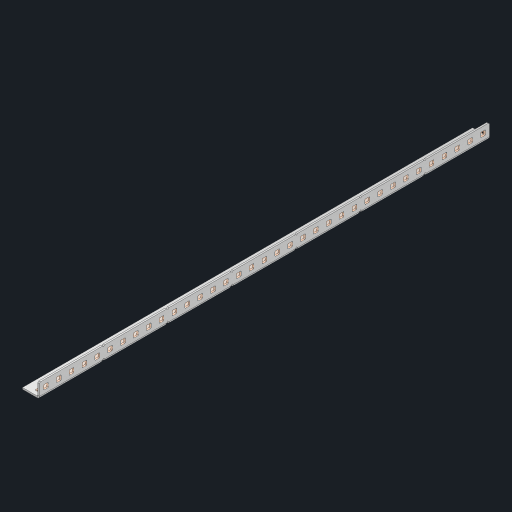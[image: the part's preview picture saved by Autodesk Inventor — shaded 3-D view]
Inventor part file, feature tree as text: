
AUTODESK INVENTOR PART (.ipt)
format: ipt  version: 2023 (Build 270158000, 158)  size: 1,058,816 bytes
history: native  units: in
note: dims shown in document units (in); Inventor stores cm internally (conversion verified against a paired STEP export)
features: other x75, extrude x69, sheet_metal_op x10, sketch x8, mirror x1, pattern_linear x1, chamfer x1
ambient origin geometry x8: Origin, YZ Plane, XZ Plane, XY Plane, X Axis, Y Axis, Z Axis, Center Point
bodies: Solid1 (feature_tree), Body (feature_tree)
feature tree (165):
  other  "Flange Pattern Plane"
  sheet_metal_op  "Flange Pattern"
  sheet_metal_op  "Body Pattern"
  other  "Arc Length"
  mirror  "Notch Mirror"
  pattern_linear  "Notch Pattern"  Spacing1=0.25in  [1 undecoded]
  chamfer  "End Chamfer"
  extrude  "Half Cut"  Depth=0.0625in
  sketch  "Sketch1"  dims[d0=1.5in]
  other  "Plate1"
  sketch  "Sketch2"  dims[d1=17.5in]
  other  "Plate2"
  sheet_metal_op  "Bend1"
  sheet_metal_op  "Corner1"
  sketch  "Sketch3"  dims[d2=0.0625in]
  other  "Flange Pattern Sketch"
  sketch  "Sketch7"  dims[d3=0.0625in]
  other  "Srf1"
  other  "Srf2"
  sketch  "Sketch8"  dims[d4=0.0312in]
  sketch  "Sketch9"  dims[d5=0.125in]
  other  "Srf91"
  sheet_metal_op  "Body Pattern Sketch"
  other  "Srf92"
  sketch  "Sketch13"  dims[d6=0.0625in]
  sketch  "Sketch14"  dims[d7=0.5in d8=90.0deg d9=0.0312in d10=0.25in d11=0.0625in d12=0.0625in d16=0.182in d17=0.02in d18=0.0625in d19=0.0in d20=0.25in d21=0.25in d46=0.172in d47=1.0in d48=0.0in d49=0.182in d50=0.02in d51=0.25in d52=0.25in d53=0.0625in d54=0.0in d55=0.172in d56=1.0in d57=0.0in d60=13.7795in d62=0.5in d63=0.3937in d65=0.5in d85=0.1473in d86=0.1782in d88=0.04in d89=0.0625in d90=0.0in d91=0.04in d92=0.0491in d95=2.5in d96=0.04in d97=0.25in d98=45.0deg d101=0.0in d102=2.497in d131=0.5in d132=13.7795in d134=0.5in d139=0.5in]
  other  "Srf856"
  other  "Srf1310"
  other  "Srf1311"
  other  "Srf1312"
  other  "Srf1376"
  other  "Srf1377"
  other  "Srf1728"
  other  "Srf1755"
  other  "Srf1878"
  other  "Srf1879"
  other  "Srf1880"
  other  "Srf1881"
  other  "Srf1882"
  other  "Srf1883"
  other  "Srf1884"
  other  "Srf1885"
  other  "Srf1886"
  other  "Srf1887"
  other  "Srf1888"
  other  "Srf1889"
  other  "Srf1890"
  other  "Srf1891"
  other  "Srf1892"
  other  "Srf1893"
  other  "Srf1894"
  other  "Srf1895"
  other  "Srf1896"
  other  "Srf1897"
  other  "Srf1898"
  other  "Srf1899"
  other  "Srf1900"
  other  "Srf1901"
  other  "Srf1902"
  other  "Srf1903"
  other  "Srf1904"
  other  "Srf1905"
  other  "Srf1906"
  other  "Srf1942"
  other  "Srf1943"
  other  "Srf1944"
  other  "Srf1945"
  other  "Srf1946"
  other  "Srf1947"
  other  "Srf1948"
  other  "Srf1949"
  other  "Srf1950"
  other  "Srf1951"
  other  "Srf1952"
  other  "Srf1953"
  other  "Srf1954"
  other  "Srf1955"
  other  "Srf1956"
  other  "Srf1957"
  other  "Srf1958"
  other  "Srf1959"
  other  "Srf1960"
  other  "Srf1961"
  other  "Srf1962"
  other  "Srf1963"
  other  "Srf1964"
  other  "Srf1965"
  other  "Srf1966"
  other  "Srf1967"
  other  "Srf1968"
  other  "Srf1969"
  other  "Srf1970"
  sheet_metal_op  "Flange Stamp"
  sheet_metal_op  "Flange Circle"
  sheet_metal_op  "Body Stamp"
  sheet_metal_op  "Body Circle"
  sheet_metal_op  "Notch"
  extrude  "ExtrusionSrf2"  Depth=0.0625in
  extrude  "ExtrusionSrf92"  Depth=0.5in
  extrude  "ExtrusionSrf856"  Depth=0.02in
  extrude  "ExtrusionSrf1310"  Depth=0.0625in
  extrude  "ExtrusionSrf1311"  TaperAngle=0.0deg  [1 undecoded]
  extrude  "ExtrusionSrf1312"  Depth=0.5in
  extrude  "ExtrusionSrf1376"  Depth=0.5in
  extrude  "ExtrusionSrf1377"  Depth=0.5in
  extrude  "ExtrusionSrf1728"  Depth=0.5in TaperAngle=0.0deg
  extrude  "ExtrusionSrf1755"  Depth=0.5in
  extrude  "ExtrusionSrf1878"  Depth=0.02in
  extrude  "ExtrusionSrf1879"  Depth=0.5in
  extrude  "ExtrusionSrf1880"  Depth=0.5in
  extrude  "ExtrusionSrf1881"  Depth=0.0625in
  extrude  "ExtrusionSrf1882"  TaperAngle=0.0deg  [1 undecoded]
  extrude  "ExtrusionSrf1883"  Depth=0.5in
  extrude  "ExtrusionSrf1884"  Depth=0.5in TaperAngle=0.0deg
  extrude  "ExtrusionSrf1885"  Depth=0.5in
  extrude  "ExtrusionSrf1886"  Depth=0.5in
  extrude  "ExtrusionSrf1887"  Depth=0.5in
  extrude  "ExtrusionSrf1888"  Depth=0.5in
  extrude  "ExtrusionSrf1889"  Depth=0.5in
  extrude  "ExtrusionSrf1890"  Depth=0.0625in
  extrude  "ExtrusionSrf1891"  TaperAngle=0.0deg  [1 undecoded]
  extrude  "ExtrusionSrf1892"  Depth=0.5in
  extrude  "ExtrusionSrf1893"  Depth=0.5in
  extrude  "ExtrusionSrf1894"  Depth=0.5in
  extrude  "ExtrusionSrf1895"  Depth=0.5in TaperAngle=45.0deg
  extrude  "ExtrusionSrf1896"  TaperAngle=0.0deg  [1 undecoded]
  extrude  "ExtrusionSrf1897"  Depth=0.5in
  extrude  "ExtrusionSrf1898"  Depth=0.5in
  extrude  "ExtrusionSrf1899"  Depth=0.5in
  extrude  "ExtrusionSrf1900"  Depth=0.5in
  extrude  "ExtrusionSrf1901"  Depth=0.5in
  extrude  "ExtrusionSrf1902"  [1 undecoded]
  extrude  "ExtrusionSrf1903"  [1 undecoded]
  extrude  "ExtrusionSrf1904"  [1 undecoded]
  extrude  "ExtrusionSrf1905"  [1 undecoded]
  extrude  "ExtrusionSrf1906"  [1 undecoded]
  extrude  "ExtrusionSrf1942"  [1 undecoded]
  extrude  "ExtrusionSrf1943"  [1 undecoded]
  extrude  "ExtrusionSrf1944"  [1 undecoded]
  extrude  "ExtrusionSrf1945"  [1 undecoded]
  extrude  "ExtrusionSrf1946"  [1 undecoded]
  extrude  "ExtrusionSrf1947"  [1 undecoded]
  extrude  "ExtrusionSrf1948"  [1 undecoded]
  extrude  "ExtrusionSrf1949"  [1 undecoded]
  extrude  "ExtrusionSrf1950"  [1 undecoded]
  extrude  "ExtrusionSrf1951"  [1 undecoded]
  extrude  "ExtrusionSrf1952"  [1 undecoded]
  extrude  "ExtrusionSrf1953"  [1 undecoded]
  extrude  "ExtrusionSrf1954"  [1 undecoded]
  extrude  "ExtrusionSrf1955"  [1 undecoded]
  extrude  "ExtrusionSrf1956"  [1 undecoded]
  extrude  "ExtrusionSrf1957"  [1 undecoded]
  extrude  "ExtrusionSrf1958"  [1 undecoded]
  extrude  "ExtrusionSrf1959"  [1 undecoded]
  extrude  "ExtrusionSrf1960"  [1 undecoded]
  extrude  "ExtrusionSrf1961"  [1 undecoded]
  extrude  "ExtrusionSrf1962"  [1 undecoded]
  extrude  "ExtrusionSrf1963"  [1 undecoded]
  extrude  "ExtrusionSrf1964"  [1 undecoded]
  extrude  "ExtrusionSrf1965"  [1 undecoded]
  extrude  "ExtrusionSrf1966"  [1 undecoded]
  extrude  "ExtrusionSrf1967"  [1 undecoded]
  extrude  "ExtrusionSrf1968"  [1 undecoded]
  extrude  "ExtrusionSrf1969"  [1 undecoded]
  extrude  "ExtrusionSrf1970"  [1 undecoded]
note: 39 required parameter values undecoded (feature->parameter linkage not recoverable at this tier; creation-order binding heuristic only, values carry confidence <= 0.55)
